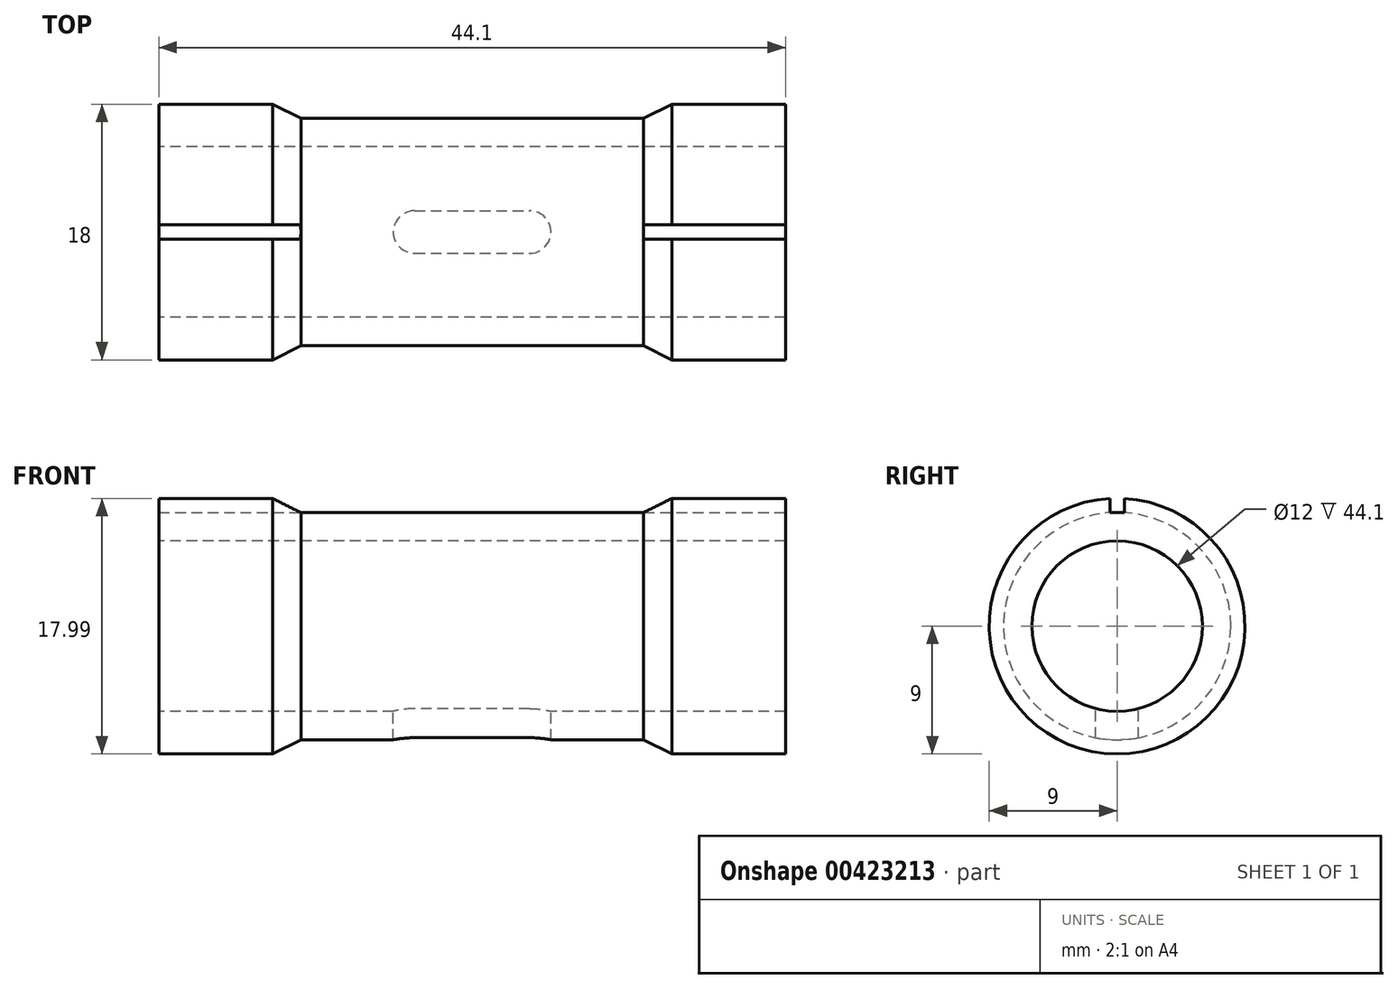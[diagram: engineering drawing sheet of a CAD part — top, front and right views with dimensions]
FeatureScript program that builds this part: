
annotation { "Feature Type Name" : "Feature", "Feature Type Description" : "" }
export const myFeature = defineFeature(function(context is Context, id is Id, definition is map)
    precondition{}
    {
        {
            var Q0;
            Q0=qCreatedBy(makeId("Right.planeOp"),FACE);
            var sketch = newSketch(context, id + "F0", { "sketchPlane" : qUnion([Q0])});
            skCircle(sketch, "E0", {"center": v(0, 0) * mm, "radius": 9 * mm});
            skSolve(sketch);
        }
        {
            var Q0;
            Q0 = qSketchRegion(id + "F0", true);
            extrude(context, id + "F1", {"entities" : qUnion([Q0]), "depth" : 10 * mm});
        }
        {
            var Q0;
            Q0=makeQuery(id+"F1.opExtrude","CAP_FACE",FACE,{"disambiguationData":[OSD([sQuery(id+"F0.wireOp",EDGE,"E0")])],"isStart":true});
            var sketch = newSketch(context, id + "F2", { "sketchPlane" : qUnion([Q0])});
            skCircle(sketch, "E1", {"center": v(0, 0) * mm, "radius": 8 * mm});
            skSolve(sketch);
        }
        {
            var Q0;
            Q0=makeQuery(id+"F2.imprint","IMPRINT",FACE,{"disambiguationData":[TD([[makeQuery(id+"F2.imprint","IMPRINT",EDGE,{"derivedFrom":sQuery(id+"F2.wireOp",EDGE,"E1")}),1.0]])]});
            extrude(context, id + "F3", {"entities" : qUnion([Q0]), "operationType" : NewBodyOperationType.ADD, "offsetDistance" : 25 * mm, "depth" : 24.1 * mm});
        }
        {
            var Q0;
            Q0=makeQuery(id+"F3.opExtrude","CAP_FACE",FACE,{"disambiguationData":[OSD([sQuery(id+"F2.wireOp",EDGE,"E1")])],"isStart":false});
            var sketch = newSketch(context, id + "F4", { "sketchPlane" : qUnion([Q0])});
            skCircle(sketch, "E2", {"center": v(0, 0) * mm, "radius": 9 * mm});
            skSolve(sketch);
        }
        {
            var Q0;
            Q0 = qSketchRegion(id + "F4", true);
            extrude(context, id + "F5", {"entities" : qUnion([Q0]), "operationType" : NewBodyOperationType.ADD, "depth" : 10 * mm});
        }
        {
            var Q0;
            Q0=makeQuery(id+"F1.opExtrude","CAP_EDGE",EDGE,{"disambiguationData":[OSD([sQuery(id+"F0.wireOp",EDGE,"E0")])],"isStart":true});
            var Q1;
            Q1=makeQuery(id+"F5.opExtrude","CAP_EDGE",EDGE,{"disambiguationData":[OSD([sQuery(id+"F4.wireOp",EDGE,"E2")])],"isStart":true});
            chamfer(context, id + "F6", {"entities" : qUnion([Q0, Q1]), "chamferType" : ChamferType.TWO_OFFSETS, "width1" : 2 * mm, "oppositeDirection" : false, "width2" : 1 * mm, "tangentPropagation" : true});
        }
        {
            var Q0;
            Q0=makeQuery(id+"F1.opExtrude","CAP_FACE",FACE,{"disambiguationData":[OSD([sQuery(id+"F0.wireOp",EDGE,"E0")])],"isStart":false});
            var sketch = newSketch(context, id + "F7", { "sketchPlane" : qUnion([Q0])});
            skLineSegment(sketch, "E3.bottom", {"start": v(-0.5, 10) * mm, "end": v(0.5, 10) * mm});
            skLineSegment(sketch, "E3.top", {"start": v(-0.5, 8) * mm, "end": v(0.5, 8) * mm});
            skLineSegment(sketch, "E3.left", {"start": v(-0.5, 10) * mm, "end": v(-0.5, 8) * mm});
            skLineSegment(sketch, "E3.right", {"start": v(0.5, 10) * mm, "end": v(0.5, 8) * mm});
            skPoint(sketch, "E3.middle", {"position": v(0, 9) * mm});
            skSolve(sketch);
        }
        {
            var Q0;
            {var subQ0=sQuery(id+"F7.wireOp",EDGE,"E3.top");Q0=makeQuery(id+"F7.imprint","IMPRINT",FACE,{"disambiguationData":[TD([[makeQuery(id+"F7.imprint","IMPRINT",EDGE,{"derivedFrom":subQ0}),1.0]])]});}
            extrude(context, id + "F8", {"entities" : qUnion([Q0]), "operationType" : NewBodyOperationType.REMOVE, "oppositeDirection" : true, "depth" : 200 * mm});
        }
        {
            var Q0;
            Q0=qCreatedBy(makeId("Top.planeOp"),FACE);
            var sketch = newSketch(context, id + "F9", { "sketchPlane" : qUnion([Q0])});
            skPoint(sketch, "E4.middle", {"position": v(-14.25, 0) * mm});
            skCircle(sketch, "E5", {"center": v(-8, 0) * mm, "radius": 1.5 * mm});
            skPoint(sketch, "E5.first.point", {"position": v(-6.5, 0) * mm});
            skPoint(sketch, "E5.third.point", {"position": v(-8, -1.5) * mm});
            skCircle(sketch, "E6", {"center": v(-16.1, 0) * mm, "radius": 1.5 * mm});
            skPoint(sketch, "E6.second.point", {"position": v(-17.6, 0) * mm});
            skPoint(sketch, "E6.third.point", {"position": v(-16.1, -1.5) * mm});
            skLineSegment(sketch, "E7", {"start": v(-8, 1.5) * mm, "end": v(-16.1, 1.5) * mm});
            skLineSegment(sketch, "E8", {"start": v(-8, -1.5) * mm, "end": v(-16.1, -1.5) * mm});
            skLineSegment(sketch, "E9", {"start": v(0, 0) * mm, "end": v(-8, 0) * mm});
            skLineSegment(sketch, "E10", {"start": v(-16.1, 0) * mm, "end": v(-8, 0) * mm});
            skLineSegment(sketch, "E11", {"start": v(-16.1, 0) * mm, "end": v(-24.1, 0) * mm});
            skSolve(sketch);
        }
        {
            var Q0;
            Q0 = qSketchRegion(id + "F9", true);
            extrude(context, id + "F10", {"entities" : qUnion([Q0]), "operationType" : NewBodyOperationType.REMOVE, "oppositeDirection" : true, "depth" : 25 * mm});
        }
        {
            var Q0;
            Q0=makeQuery(id+"F5.opExtrude","CAP_FACE",FACE,{"disambiguationData":[OSD([sQuery(id+"F4.wireOp",EDGE,"E2")])],"isStart":false});
            var sketch = newSketch(context, id + "F11", { "sketchPlane" : qUnion([Q0])});
            skCircle(sketch, "E12", {"center": v(0, 0) * mm, "radius": 6 * mm});
            skSolve(sketch);
        }
        {
            var Q0;
            Q0 = qSketchRegion(id + "F11", true);
            extrude(context, id + "F12", {"entities" : qUnion([Q0]), "operationType" : NewBodyOperationType.REMOVE, "oppositeDirection" : true, "depth" : 53.9 * mm, "offsetDistance" : 25 * mm});
        }
    });
